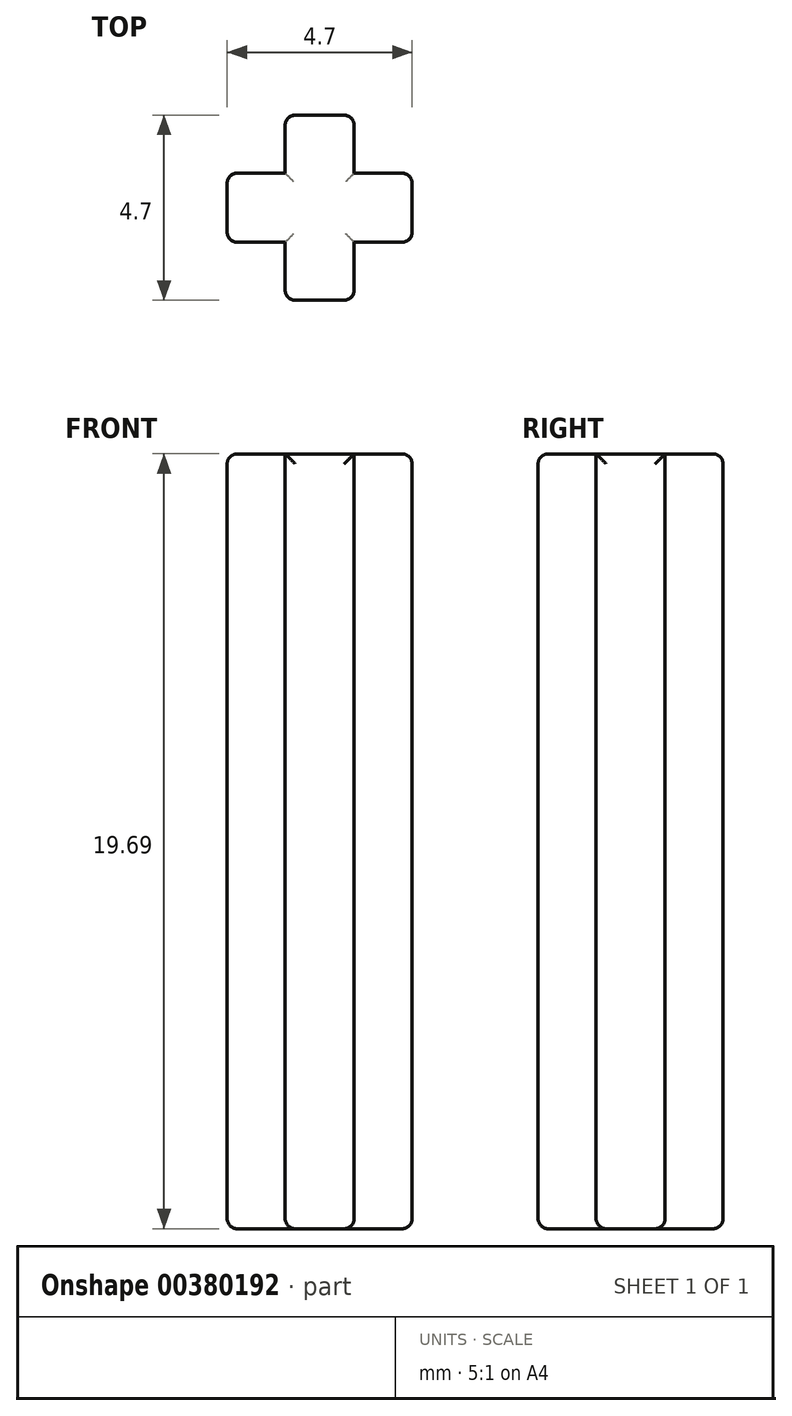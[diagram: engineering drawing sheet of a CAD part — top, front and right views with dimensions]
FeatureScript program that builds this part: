
annotation { "Feature Type Name" : "Feature", "Feature Type Description" : "" }
export const myFeature = defineFeature(function(context is Context, id is Id, definition is map)
    precondition{}
    {
        {
            var Q0;
            Q0=qCreatedBy(makeId("Top.planeOp"),FACE);
            var sketch = newSketch(context, id + "F0", { "sketchPlane" : qUnion([Q0])});
            skLineSegment(sketch, "E0", {"start": v(-2.35, 0) * mm, "end": v(-2.35, 0.88) * mm});
            skLineSegment(sketch, "E1", {"start": v(-2.35, 0.88) * mm, "end": v(-0.88, 0.88) * mm});
            skLineSegment(sketch, "E2", {"start": v(-0.88, 0.88) * mm, "end": v(-0.88, 2.35) * mm});
            skLineSegment(sketch, "E3", {"start": v(-0.88, 2.35) * mm, "end": v(0, 2.35) * mm});
            skLineSegment(sketch, "E4.MirrorCS", {"start": v(2.35, 0.88) * mm, "end": v(0.88, 0.88) * mm});
            skLineSegment(sketch, "E5.MirrorCS", {"start": v(0.88, 0.88) * mm, "end": v(0.88, 2.35) * mm});
            skLineSegment(sketch, "E6.MirrorCS", {"start": v(2.35, 0) * mm, "end": v(2.35, 0.88) * mm});
            skLineSegment(sketch, "E7.MirrorCS", {"start": v(0.88, 2.35) * mm, "end": v(0, 2.35) * mm});
            skLineSegment(sketch, "E8.MirrorCS", {"start": v(0.88, -2.35) * mm, "end": v(0, -2.35) * mm});
            skLineSegment(sketch, "E9.MirrorCS", {"start": v(0.88, -0.88) * mm, "end": v(0.88, -2.35) * mm});
            skLineSegment(sketch, "E10.MirrorCS", {"start": v(-0.88, -2.35) * mm, "end": v(0, -2.35) * mm});
            skLineSegment(sketch, "E11.MirrorCS", {"start": v(-0.88, -0.88) * mm, "end": v(-0.88, -2.35) * mm});
            skLineSegment(sketch, "E12.MirrorCS", {"start": v(2.35, -0.88) * mm, "end": v(0.88, -0.88) * mm});
            skLineSegment(sketch, "E13.MirrorCS", {"start": v(-2.35, -0.88) * mm, "end": v(-0.88, -0.88) * mm});
            skLineSegment(sketch, "E14.MirrorCS", {"start": v(2.35, 0) * mm, "end": v(2.35, -0.88) * mm});
            skLineSegment(sketch, "E15.MirrorCS", {"start": v(-2.35, 0) * mm, "end": v(-2.35, -0.88) * mm});
            skSolve(sketch);
        }
        {
            var Q0;
            Q0=makeQuery(id+"F0.imprint","IMPRINT",FACE,{"disambiguationData":[TD([[makeQuery(id+"F0.imprint","IMPRINT",EDGE,{"derivedFrom":sQuery(id+"F0.wireOp",EDGE,"E0")}),-1.0]])]});
            extrude(context, id + "F1", {"entities" : qUnion([Q0]), "depth" : 19.68 * mm});
        }
        {
            var Q0;
            Q0=makeQuery(id+"F1.opExtrude","CAP_FACE",FACE,{"disambiguationData":[OSD([sQuery(id+"F0.wireOp",EDGE,"E0"),sQuery(id+"F0.wireOp",EDGE,"E1"),sQuery(id+"F0.wireOp",EDGE,"E2"),sQuery(id+"F0.wireOp",EDGE,"E3"),sQuery(id+"F0.wireOp",EDGE,"E4.MirrorCS"),sQuery(id+"F0.wireOp",EDGE,"E5.MirrorCS"),sQuery(id+"F0.wireOp",EDGE,"E6.MirrorCS"),sQuery(id+"F0.wireOp",EDGE,"E7.MirrorCS"),sQuery(id+"F0.wireOp",EDGE,"E8.MirrorCS"),sQuery(id+"F0.wireOp",EDGE,"E9.MirrorCS"),sQuery(id+"F0.wireOp",EDGE,"E10.MirrorCS"),sQuery(id+"F0.wireOp",EDGE,"E11.MirrorCS"),sQuery(id+"F0.wireOp",EDGE,"E12.MirrorCS"),sQuery(id+"F0.wireOp",EDGE,"E13.MirrorCS"),sQuery(id+"F0.wireOp",EDGE,"E14.MirrorCS"),sQuery(id+"F0.wireOp",EDGE,"E15.MirrorCS")])],"isStart":true});
            var Q1;
            Q1=makeQuery(id+"F1.opExtrude","SWEPT_FACE",FACE,{"disambiguationData":[OSD([sQuery(id+"F0.wireOp",EDGE,"E0"),sQuery(id+"F0.wireOp",EDGE,"E15.MirrorCS")])]});
            var Q2;
            Q2=makeQuery(id+"F1.opExtrude","SWEPT_FACE",FACE,{"disambiguationData":[OSD([sQuery(id+"F0.wireOp",EDGE,"E3"),sQuery(id+"F0.wireOp",EDGE,"E7.MirrorCS")])]});
            var Q3;
            Q3=makeQuery(id+"F1.opExtrude","SWEPT_FACE",FACE,{"disambiguationData":[OSD([sQuery(id+"F0.wireOp",EDGE,"E6.MirrorCS"),sQuery(id+"F0.wireOp",EDGE,"E14.MirrorCS")])]});
            var Q4;
            Q4=makeQuery(id+"F1.opExtrude","SWEPT_FACE",FACE,{"disambiguationData":[OSD([sQuery(id+"F0.wireOp",EDGE,"E8.MirrorCS"),sQuery(id+"F0.wireOp",EDGE,"E10.MirrorCS")])]});
            fillet(context, id + "F2", {"entities" : qUnion([Q0, Q1, Q2, Q3, Q4]), "radius" : 0.25 * mm, "tangentPropagation" : true, "allowEdgeOverflow" : false});
        }
    });
